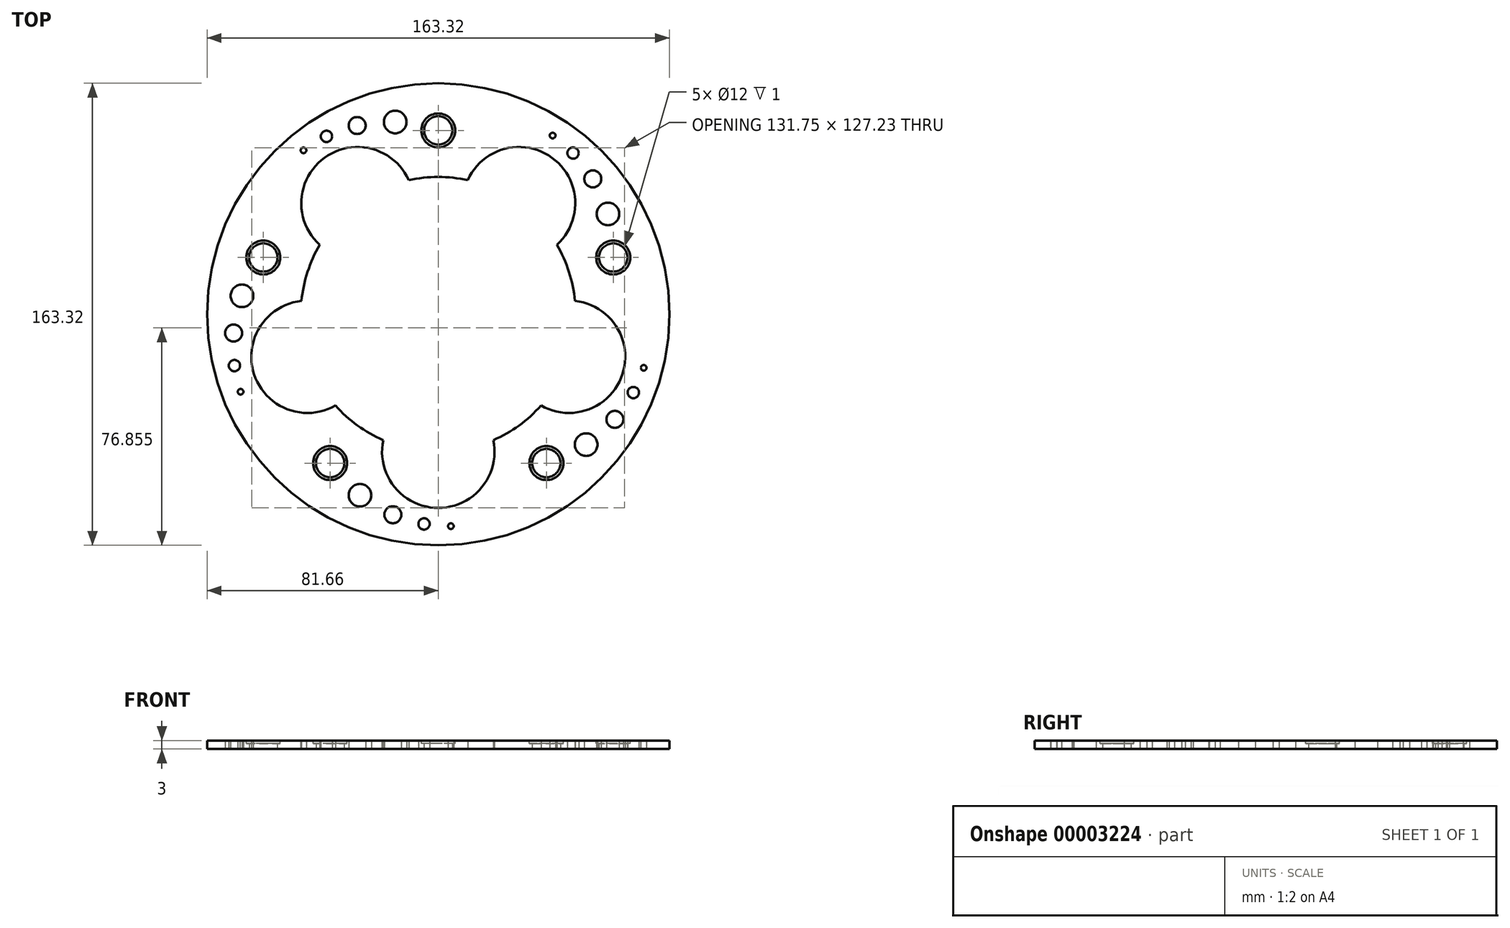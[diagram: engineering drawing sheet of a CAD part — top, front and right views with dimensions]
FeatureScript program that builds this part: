
annotation { "Feature Type Name" : "Feature", "Feature Type Description" : "" }
export const myFeature = defineFeature(function(context is Context, id is Id, definition is map)
    precondition{}
    {
        {
            var Q0;
            Q0=qCreatedBy(makeId("Top.planeOp"),FACE);
            var sketch = newSketch(context, id + "F0", { "sketchPlane" : qUnion([Q0])});
            skCircle(sketch, "E0", {"center": v(0, 0) * mm, "radius": 65 * mm});
            skCircle(sketch, "E1", {"center": v(0, 65) * mm, "radius": 5 * mm});
            skSolve(sketch);
        }
        {
            var Q0;
            {var subQ0=sQuery(id+"F0.wireOp",EDGE,"E1");var subQ1=sQuery(id+"F0.wireOp",EDGE,"E0");var subQ3=makeQuery(id+"F0.imprint","INTERSECT",VERTEX,{"disambiguationData":[OD(0.0)],"derivedFrom":[subQ1,subQ0]});var subQ4=makeQuery(id+"F0.imprint","IMPRINT",EDGE,{"disambiguationData":[TD([[subQ3,1.0]])],"derivedFrom":subQ1});Q0=qUnion([makeQuery(id+"F0.imprint","IMPRINT",FACE,{"disambiguationData":[TD([[subQ4,-1.0]])]}),makeQuery(id+"F0.imprint","IMPRINT",FACE,{"disambiguationData":[TD([[makeQuery(id+"F0.imprint","IMPRINT",EDGE,{"disambiguationData":[TD([[subQ3,-1.0]])],"derivedFrom":subQ1}),1.0]])]}),makeQuery(id+"F0.imprint","IMPRINT",FACE,{"disambiguationData":[TD([[subQ4,1.0]])]})]);}
            var sketch = newSketch(context, id + "F1", { "sketchPlane" : qUnion([Q0])});
            skArc(sketch, "E2", {"start": v(-41.88, 24.57) * mm, "mid": v(-46.18, 15) * mm, "end": v(-48.32, 4.74) * mm});
            skCircle(sketch, "E3", {"center": v(0, 0) * mm, "radius": 81.66 * mm});
            skArc(sketch, "E4", {"start": v(41.88, 24.57) * mm, "mid": v(40.22, 55.35) * mm, "end": v(10.42, 47.42) * mm});
            skArc(sketch, "E5.0.MirrorC", {"start": v(-41.88, 24.57) * mm, "mid": v(-40.22, 55.35) * mm, "end": v(-10.42, 47.42) * mm});
            skArc(sketch, "E6.0.MirrorC", {"start": v(-19.44, -44.5) * mm, "mid": v(0, -68.42) * mm, "end": v(19.44, -44.5) * mm});
            skArc(sketch, "E7.0.MirrorC", {"start": v(48.32, 4.74) * mm, "mid": v(65.07, -21.14) * mm, "end": v(36.3, -32.24) * mm});
            skArc(sketch, "E8.0.MirrorC", {"start": v(-36.3, -32.24) * mm, "mid": v(-65.07, -21.14) * mm, "end": v(-48.32, 4.74) * mm});
            skArc(sketch, "E9.trimOffspring", {"start": v(-36.3, -32.24) * mm, "mid": v(-28.54, -39.28) * mm, "end": v(-19.44, -44.5) * mm});
            skArc(sketch, "E10.trimOffspring", {"start": v(19.44, -44.5) * mm, "mid": v(28.54, -39.28) * mm, "end": v(36.3, -32.24) * mm});
            skArc(sketch, "E11.trimOffspring", {"start": v(48.32, 4.74) * mm, "mid": v(46.18, 15) * mm, "end": v(41.88, 24.57) * mm});
            skArc(sketch, "E12.trimOffspring", {"start": v(10.42, 47.42) * mm, "mid": v(0, 48.56) * mm, "end": v(-10.42, 47.42) * mm});
            skPoint(sketch, "E13.orphan", {"position": v(0, 103.8) * mm});
            skLineSegment(sketch, "E14", {"start": v(0, 0) * mm, "end": v(0, 65) * mm});
            skCircle(sketch, "E15", {"center": v(0, 65) * mm, "radius": 5 * mm});
            skCircle(sketch, "E16", {"center": v(-17.26, 17.2) * mm, "radius": 50.82 * mm, "construction": true});
            skCircle(sketch, "E17", {"center": v(-15.21, 67.98) * mm, "radius": 4 * mm});
            skCircle(sketch, "E18", {"center": v(-28.65, 66.73) * mm, "radius": 3 * mm});
            skCircle(sketch, "E19", {"center": v(-39.5, 62.9) * mm, "radius": 2 * mm});
            skCircle(sketch, "E20", {"center": v(-47.61, 57.96) * mm, "radius": 1 * mm});
            skPoint(sketch, "E21.orphan", {"position": v(-51.3, 63.54) * mm});
            skPoint(sketch, "E22.trimOffspring.end.orphan", {"position": v(-49.46, 60.75) * mm});
            skLineSegment(sketch, "E23", {"start": v(0, 0) * mm, "end": v(28.54, 39.28) * mm});
            skLineSegment(sketch, "E24", {"start": v(0, 0) * mm, "end": v(-28.54, 39.28) * mm});
            skLineSegment(sketch, "E25", {"start": v(0, 0) * mm, "end": v(-46.18, -15) * mm});
            skLineSegment(sketch, "E26", {"start": v(0, 0) * mm, "end": v(46.18, -15) * mm});
            skLineSegment(sketch, "E27", {"start": v(0, 0) * mm, "end": v(0, -48.56) * mm});
            skSolve(sketch);
        }
        {
            var Q0;
            {var subQ5=sQuery(id+"F1.wireOp",EDGE,"E14");var subQ7=sQuery(id+"F1.wireOp",EDGE,"E15");var subQ9=makeQuery(id+"F1.imprint","INTERSECT",VERTEX,{"derivedFrom":[subQ5,subQ7]});Q0=makeQuery(id+"F1.imprint","IMPRINT",FACE,{"disambiguationData":[TD([[makeQuery(id+"F1.imprint","IMPRINT",EDGE,{"disambiguationData":[TD([[subQ9,-1.0]])],"derivedFrom":subQ5}),1.0]])]});}
            var Q1;
            {var subQ0=sQuery(id+"F0.wireOp",EDGE,"E0");var subQ1=sQuery(id+"F0.wireOp",EDGE,"E1");var subQ3=makeQuery(id+"F0.imprint","INTERSECT",VERTEX,{"disambiguationData":[OD(0.0)],"derivedFrom":[subQ0,subQ1]});var subQ4=makeQuery(id+"F0.imprint","IMPRINT",EDGE,{"disambiguationData":[TD([[subQ3,1.0]])],"derivedFrom":subQ0});var subQ5=makeQuery(id+"F1.imprint","INTERSECT",VERTEX,{"derivedFrom":[subQ4,sQuery(id+"F1.wireOp",EDGE,"E14")]});Q1=makeQuery(id+"F1.imprint","IMPRINT",FACE,{"disambiguationData":[TD([[makeQuery(id+"F1.imprint","IMPRINT",EDGE,{"disambiguationData":[TD([[subQ5,-1.0]])],"derivedFrom":subQ4}),-1.0]])]});}
            var Q2;
            {var subQ5=sQuery(id+"F1.wireOp",EDGE,"E14");var subQ7=sQuery(id+"F1.wireOp",EDGE,"E15");var subQ9=makeQuery(id+"F1.imprint","INTERSECT",VERTEX,{"derivedFrom":[subQ5,subQ7]});Q2=makeQuery(id+"F1.imprint","IMPRINT",FACE,{"disambiguationData":[TD([[makeQuery(id+"F1.imprint","IMPRINT",EDGE,{"disambiguationData":[TD([[subQ9,-1.0]])],"derivedFrom":subQ5}),-1.0]])]});}
            var Q3;
            Q3=makeQuery(id+"F1.imprint","IMPRINT",FACE,{"disambiguationData":[TD([[makeQuery(id+"F1.imprint","IMPRINT",EDGE,{"derivedFrom":sQuery(id+"F1.wireOp",EDGE,"E17")}),1.0]])]});
            var Q4;
            Q4=makeQuery(id+"F1.imprint","IMPRINT",FACE,{"disambiguationData":[TD([[makeQuery(id+"F1.imprint","IMPRINT",EDGE,{"derivedFrom":sQuery(id+"F1.wireOp",EDGE,"E18")}),1.0]])]});
            var Q5;
            Q5=makeQuery(id+"F1.imprint","IMPRINT",FACE,{"disambiguationData":[TD([[makeQuery(id+"F1.imprint","IMPRINT",EDGE,{"derivedFrom":sQuery(id+"F1.wireOp",EDGE,"E19")}),1.0]])]});
            var Q6;
            Q6=makeQuery(id+"F1.imprint","IMPRINT",FACE,{"disambiguationData":[TD([[makeQuery(id+"F1.imprint","IMPRINT",EDGE,{"derivedFrom":sQuery(id+"F1.wireOp",EDGE,"E20")}),1.0]])]});
            extrude(context, id + "F2", {"entities" : qUnion([Q0, Q1, Q2, Q3, Q4, Q5, Q6]), "depth" : 25 * mm});
        }
        {
            var Q0;
            Q0=makeQuery(id+"F2.opExtrude","SWEPT_BODY",BODY,{"disambiguationData":[OSD([sQuery(id+"F1.wireOp",EDGE,"E15")])]});
            var Q1;
            Q1=makeQuery(id+"F2.opExtrude","SWEPT_BODY",BODY,{"disambiguationData":[OSD([sQuery(id+"F1.wireOp",EDGE,"E17")])]});
            var Q2;
            Q2=makeQuery(id+"F2.opExtrude","SWEPT_BODY",BODY,{"disambiguationData":[OSD([sQuery(id+"F1.wireOp",EDGE,"E18")])]});
            var Q3;
            Q3=makeQuery(id+"F2.opExtrude","SWEPT_BODY",BODY,{"disambiguationData":[OSD([sQuery(id+"F1.wireOp",EDGE,"E19")])]});
            var Q4;
            Q4=makeQuery(id+"F2.opExtrude","SWEPT_BODY",BODY,{"disambiguationData":[OSD([sQuery(id+"F1.wireOp",EDGE,"E20")])]});
            var Q5;
            Q5=sQuery(id+"F1.wireOp",EDGE,"E3");
            circularPattern(context, id + "F3", {"entities" : qUnion([Q0, Q1, Q2, Q3, Q4]), "axis" : qUnion([Q5]), "angle" : 72 * degree, "instanceCount" : 5});
        }
        {
            var Q0;
            Q0=makeQuery(id+"F1.imprint","IMPRINT",FACE,{"disambiguationData":[TD([[makeQuery(id+"F1.imprint","IMPRINT",EDGE,{"derivedFrom":sQuery(id+"F1.wireOp",EDGE,"E3")}),1.0]])]});
            var Q1;
            {var subQ9=sQuery(id+"F1.wireOp",EDGE,"E4");var subQ11=sQuery(id+"F1.wireOp",EDGE,"E12.trimOffspring");var subQ13=makeQuery(id+"F1.imprint","INTERSECT",VERTEX,{"derivedFrom":[subQ9,subQ11]});Q1=makeQuery(id+"F1.imprint","IMPRINT",FACE,{"disambiguationData":[TD([[makeQuery(id+"F1.imprint","IMPRINT",EDGE,{"disambiguationData":[TD([[subQ13,-1.0]])],"derivedFrom":subQ11}),-1.0]])]});}
            var Q2;
            {var subQ5=sQuery(id+"F1.wireOp",EDGE,"E5.0.MirrorC");var subQ11=sQuery(id+"F1.wireOp",EDGE,"E12.trimOffspring");var subQ13=makeQuery(id+"F1.imprint","INTERSECT",VERTEX,{"derivedFrom":[subQ5,subQ11]});Q2=makeQuery(id+"F1.imprint","IMPRINT",FACE,{"disambiguationData":[TD([[makeQuery(id+"F1.imprint","IMPRINT",EDGE,{"disambiguationData":[TD([[subQ13,1.0]])],"derivedFrom":subQ11}),-1.0]])]});}
            var Q3;
            {var subQ7=sQuery(id+"F1.wireOp",EDGE,"E2");Q3=makeQuery(id+"F1.imprint","IMPRINT",FACE,{"disambiguationData":[TD([[makeQuery(id+"F1.imprint","IMPRINT",EDGE,{"derivedFrom":subQ7}),-1.0]])]});}
            var Q4;
            {var subQ7=sQuery(id+"F1.wireOp",EDGE,"E9.trimOffspring");Q4=makeQuery(id+"F1.imprint","IMPRINT",FACE,{"disambiguationData":[TD([[makeQuery(id+"F1.imprint","IMPRINT",EDGE,{"derivedFrom":subQ7}),-1.0]])]});}
            var Q5;
            {var subQ7=sQuery(id+"F1.wireOp",EDGE,"E10.trimOffspring");Q5=makeQuery(id+"F1.imprint","IMPRINT",FACE,{"disambiguationData":[TD([[makeQuery(id+"F1.imprint","IMPRINT",EDGE,{"derivedFrom":subQ7}),-1.0]])]});}
            var Q6;
            {var subQ7=sQuery(id+"F1.wireOp",EDGE,"E11.trimOffspring");Q6=makeQuery(id+"F1.imprint","IMPRINT",FACE,{"disambiguationData":[TD([[makeQuery(id+"F1.imprint","IMPRINT",EDGE,{"derivedFrom":subQ7}),-1.0]])]});}
            extrude(context, id + "F4", {"entities" : qUnion([Q0, Q1, Q2, Q3, Q4, Q5, Q6]), "depth" : 3 * mm});
        }
        {
            var Q0;
            Q0=makeQuery(id+"F3.opPattern","COPY",BODY,{"derivedFrom":makeQuery(id+"F2.opExtrude","SWEPT_BODY",BODY,{"disambiguationData":[OSD([sQuery(id+"F1.wireOp",EDGE,"E15")])]}),"instanceName":"3"});
            var Q1;
            Q1=makeQuery(id+"F3.opPattern","COPY",BODY,{"derivedFrom":makeQuery(id+"F2.opExtrude","SWEPT_BODY",BODY,{"disambiguationData":[OSD([sQuery(id+"F1.wireOp",EDGE,"E17")])]}),"instanceName":"3"});
            var Q2;
            Q2=makeQuery(id+"F3.opPattern","COPY",BODY,{"derivedFrom":makeQuery(id+"F2.opExtrude","SWEPT_BODY",BODY,{"disambiguationData":[OSD([sQuery(id+"F1.wireOp",EDGE,"E18")])]}),"instanceName":"3"});
            var Q3;
            Q3=makeQuery(id+"F3.opPattern","COPY",BODY,{"derivedFrom":makeQuery(id+"F2.opExtrude","SWEPT_BODY",BODY,{"disambiguationData":[OSD([sQuery(id+"F1.wireOp",EDGE,"E19")])]}),"instanceName":"3"});
            var Q4;
            Q4=makeQuery(id+"F3.opPattern","COPY",BODY,{"derivedFrom":makeQuery(id+"F2.opExtrude","SWEPT_BODY",BODY,{"disambiguationData":[OSD([sQuery(id+"F1.wireOp",EDGE,"E20")])]}),"instanceName":"3"});
            var Q5;
            Q5=makeQuery(id+"F3.opPattern","COPY",BODY,{"derivedFrom":makeQuery(id+"F2.opExtrude","SWEPT_BODY",BODY,{"disambiguationData":[OSD([sQuery(id+"F1.wireOp",EDGE,"E15")])]}),"instanceName":"4"});
            var Q6;
            Q6=makeQuery(id+"F3.opPattern","COPY",BODY,{"derivedFrom":makeQuery(id+"F2.opExtrude","SWEPT_BODY",BODY,{"disambiguationData":[OSD([sQuery(id+"F1.wireOp",EDGE,"E17")])]}),"instanceName":"4"});
            var Q7;
            Q7=makeQuery(id+"F3.opPattern","COPY",BODY,{"derivedFrom":makeQuery(id+"F2.opExtrude","SWEPT_BODY",BODY,{"disambiguationData":[OSD([sQuery(id+"F1.wireOp",EDGE,"E18")])]}),"instanceName":"4"});
            var Q8;
            Q8=makeQuery(id+"F3.opPattern","COPY",BODY,{"derivedFrom":makeQuery(id+"F2.opExtrude","SWEPT_BODY",BODY,{"disambiguationData":[OSD([sQuery(id+"F1.wireOp",EDGE,"E19")])]}),"instanceName":"4"});
            var Q9;
            Q9=makeQuery(id+"F3.opPattern","COPY",BODY,{"derivedFrom":makeQuery(id+"F2.opExtrude","SWEPT_BODY",BODY,{"disambiguationData":[OSD([sQuery(id+"F1.wireOp",EDGE,"E20")])]}),"instanceName":"4"});
            var Q10;
            Q10=makeQuery(id+"F2.opExtrude","SWEPT_BODY",BODY,{"disambiguationData":[OSD([sQuery(id+"F1.wireOp",EDGE,"E15")])]});
            var Q11;
            Q11=makeQuery(id+"F2.opExtrude","SWEPT_BODY",BODY,{"disambiguationData":[OSD([sQuery(id+"F1.wireOp",EDGE,"E17")])]});
            var Q12;
            Q12=makeQuery(id+"F2.opExtrude","SWEPT_BODY",BODY,{"disambiguationData":[OSD([sQuery(id+"F1.wireOp",EDGE,"E18")])]});
            var Q13;
            Q13=makeQuery(id+"F2.opExtrude","SWEPT_BODY",BODY,{"disambiguationData":[OSD([sQuery(id+"F1.wireOp",EDGE,"E19")])]});
            var Q14;
            Q14=makeQuery(id+"F2.opExtrude","SWEPT_BODY",BODY,{"disambiguationData":[OSD([sQuery(id+"F1.wireOp",EDGE,"E20")])]});
            var Q15;
            Q15=makeQuery(id+"F3.opPattern","COPY",BODY,{"derivedFrom":makeQuery(id+"F2.opExtrude","SWEPT_BODY",BODY,{"disambiguationData":[OSD([sQuery(id+"F1.wireOp",EDGE,"E15")])]}),"instanceName":"1"});
            var Q16;
            Q16=makeQuery(id+"F3.opPattern","COPY",BODY,{"derivedFrom":makeQuery(id+"F2.opExtrude","SWEPT_BODY",BODY,{"disambiguationData":[OSD([sQuery(id+"F1.wireOp",EDGE,"E17")])]}),"instanceName":"1"});
            var Q17;
            Q17=makeQuery(id+"F3.opPattern","COPY",BODY,{"derivedFrom":makeQuery(id+"F2.opExtrude","SWEPT_BODY",BODY,{"disambiguationData":[OSD([sQuery(id+"F1.wireOp",EDGE,"E18")])]}),"instanceName":"1"});
            var Q18;
            Q18=makeQuery(id+"F3.opPattern","COPY",BODY,{"derivedFrom":makeQuery(id+"F2.opExtrude","SWEPT_BODY",BODY,{"disambiguationData":[OSD([sQuery(id+"F1.wireOp",EDGE,"E19")])]}),"instanceName":"1"});
            var Q19;
            Q19=makeQuery(id+"F3.opPattern","COPY",BODY,{"derivedFrom":makeQuery(id+"F2.opExtrude","SWEPT_BODY",BODY,{"disambiguationData":[OSD([sQuery(id+"F1.wireOp",EDGE,"E20")])]}),"instanceName":"1"});
            var Q20;
            Q20=makeQuery(id+"F3.opPattern","COPY",BODY,{"derivedFrom":makeQuery(id+"F2.opExtrude","SWEPT_BODY",BODY,{"disambiguationData":[OSD([sQuery(id+"F1.wireOp",EDGE,"E15")])]}),"instanceName":"2"});
            var Q21;
            Q21=makeQuery(id+"F3.opPattern","COPY",BODY,{"derivedFrom":makeQuery(id+"F2.opExtrude","SWEPT_BODY",BODY,{"disambiguationData":[OSD([sQuery(id+"F1.wireOp",EDGE,"E17")])]}),"instanceName":"2"});
            var Q22;
            Q22=makeQuery(id+"F3.opPattern","COPY",BODY,{"derivedFrom":makeQuery(id+"F2.opExtrude","SWEPT_BODY",BODY,{"disambiguationData":[OSD([sQuery(id+"F1.wireOp",EDGE,"E18")])]}),"instanceName":"2"});
            var Q23;
            Q23=makeQuery(id+"F3.opPattern","COPY",BODY,{"derivedFrom":makeQuery(id+"F2.opExtrude","SWEPT_BODY",BODY,{"disambiguationData":[OSD([sQuery(id+"F1.wireOp",EDGE,"E19")])]}),"instanceName":"2"});
            var Q24;
            Q24=makeQuery(id+"F3.opPattern","COPY",BODY,{"derivedFrom":makeQuery(id+"F2.opExtrude","SWEPT_BODY",BODY,{"disambiguationData":[OSD([sQuery(id+"F1.wireOp",EDGE,"E20")])]}),"instanceName":"2"});
            var Q25;
            Q25=makeQuery(id+"F4.opExtrude","SWEPT_BODY",BODY,{"disambiguationData":[OSD([sQuery(id+"F1.wireOp",EDGE,"E2"),sQuery(id+"F1.wireOp",EDGE,"E3"),sQuery(id+"F1.wireOp",EDGE,"E4"),sQuery(id+"F1.wireOp",EDGE,"E5.0.MirrorC"),sQuery(id+"F1.wireOp",EDGE,"E6.0.MirrorC"),sQuery(id+"F1.wireOp",EDGE,"E7.0.MirrorC"),sQuery(id+"F1.wireOp",EDGE,"E8.0.MirrorC"),sQuery(id+"F1.wireOp",EDGE,"E9.trimOffspring"),sQuery(id+"F1.wireOp",EDGE,"E10.trimOffspring"),sQuery(id+"F1.wireOp",EDGE,"E11.trimOffspring"),sQuery(id+"F1.wireOp",EDGE,"E12.trimOffspring"),sQuery(id+"F1.wireOp",EDGE,"E15"),sQuery(id+"F1.wireOp",EDGE,"E17"),sQuery(id+"F1.wireOp",EDGE,"E18"),sQuery(id+"F1.wireOp",EDGE,"E19"),sQuery(id+"F1.wireOp",EDGE,"E20")])]});
            booleanBodies(context, id + "F5", {"operationType" : BooleanOperationType.SUBTRACTION, "tools" : qUnion([Q0, Q1, Q2, Q3, Q4, Q5, Q6, Q7, Q8, Q9, Q10, Q11, Q12, Q13, Q14, Q15, Q16, Q17, Q18, Q19, Q20, Q21, Q22, Q23, Q24]), "targets" : qUnion([Q25])});
        }
        {
            var Q0;
            Q0=makeQuery(id+"F4.opExtrude","CAP_FACE",FACE,{"disambiguationData":[OSD([sQuery(id+"F1.wireOp",EDGE,"E2"),sQuery(id+"F1.wireOp",EDGE,"E3"),sQuery(id+"F1.wireOp",EDGE,"E4"),sQuery(id+"F1.wireOp",EDGE,"E5.0.MirrorC"),sQuery(id+"F1.wireOp",EDGE,"E6.0.MirrorC"),sQuery(id+"F1.wireOp",EDGE,"E7.0.MirrorC"),sQuery(id+"F1.wireOp",EDGE,"E8.0.MirrorC"),sQuery(id+"F1.wireOp",EDGE,"E9.trimOffspring"),sQuery(id+"F1.wireOp",EDGE,"E10.trimOffspring"),sQuery(id+"F1.wireOp",EDGE,"E11.trimOffspring"),sQuery(id+"F1.wireOp",EDGE,"E12.trimOffspring"),sQuery(id+"F1.wireOp",EDGE,"E15"),sQuery(id+"F1.wireOp",EDGE,"E17"),sQuery(id+"F1.wireOp",EDGE,"E18"),sQuery(id+"F1.wireOp",EDGE,"E19"),sQuery(id+"F1.wireOp",EDGE,"E20")])],"isStart":false});
            var sketch = newSketch(context, id + "F6", { "sketchPlane" : qUnion([Q0])});
            skCircle(sketch, "E28", {"center": v(0, 65) * mm, "radius": 6 * mm});
            skSolve(sketch);
        }
        {
            var Q0;
            {var subQ0=makeQuery(id+"F6.imprint","IMPRINT",EDGE,{"derivedFrom":makeQuery(id+"F4.opExtrude","CAP_EDGE",EDGE,{"disambiguationData":[OSD([sQuery(id+"F1.wireOp",EDGE,"E15")])],"isStart":false})});Q0=qUnion([makeQuery(id+"F6.imprint","IMPRINT",FACE,{"disambiguationData":[TD([[subQ0,1.0]])]}),makeQuery(id+"F6.imprint","IMPRINT",FACE,{"disambiguationData":[TD([[makeQuery(id+"F6.imprint","IMPRINT",EDGE,{"derivedFrom":sQuery(id+"F6.wireOp",EDGE,"E28")}),1.0]])]})]);}
            extrude(context, id + "F7", {"entities" : qUnion([Q0]), "oppositeDirection" : true, "depth" : 1 * mm});
        }
        {
            var Q0;
            Q0=makeQuery(id+"F7.opExtrude","SWEPT_BODY",BODY,{"disambiguationData":[OSD([sQuery(id+"F6.wireOp",EDGE,"E28")])]});
            var Q1;
            Q1=makeQuery(id+"F4.opExtrude","CAP_EDGE",EDGE,{"disambiguationData":[OSD([sQuery(id+"F1.wireOp",EDGE,"E3")])],"isStart":false});
            circularPattern(context, id + "F8", {"entities" : qUnion([Q0]), "axis" : qUnion([Q1]), "angle" : 72 * degree, "instanceCount" : 5});
        }
        {
            var Q0;
            Q0=makeQuery(id+"F7.opExtrude","SWEPT_BODY",BODY,{"disambiguationData":[OSD([sQuery(id+"F6.wireOp",EDGE,"E28")])]});
            var Q1;
            Q1=makeQuery(id+"F8.opPattern","COPY",BODY,{"derivedFrom":makeQuery(id+"F7.opExtrude","SWEPT_BODY",BODY,{"disambiguationData":[OSD([sQuery(id+"F6.wireOp",EDGE,"E28")])]}),"instanceName":"1"});
            var Q2;
            Q2=makeQuery(id+"F8.opPattern","COPY",BODY,{"derivedFrom":makeQuery(id+"F7.opExtrude","SWEPT_BODY",BODY,{"disambiguationData":[OSD([sQuery(id+"F6.wireOp",EDGE,"E28")])]}),"instanceName":"2"});
            var Q3;
            Q3=makeQuery(id+"F8.opPattern","COPY",BODY,{"derivedFrom":makeQuery(id+"F7.opExtrude","SWEPT_BODY",BODY,{"disambiguationData":[OSD([sQuery(id+"F6.wireOp",EDGE,"E28")])]}),"instanceName":"3"});
            var Q4;
            Q4=makeQuery(id+"F8.opPattern","COPY",BODY,{"derivedFrom":makeQuery(id+"F7.opExtrude","SWEPT_BODY",BODY,{"disambiguationData":[OSD([sQuery(id+"F6.wireOp",EDGE,"E28")])]}),"instanceName":"4"});
            var Q5;
            Q5=makeQuery(id+"F4.opExtrude","SWEPT_BODY",BODY,{"disambiguationData":[OSD([sQuery(id+"F1.wireOp",EDGE,"E2"),sQuery(id+"F1.wireOp",EDGE,"E3"),sQuery(id+"F1.wireOp",EDGE,"E4"),sQuery(id+"F1.wireOp",EDGE,"E5.0.MirrorC"),sQuery(id+"F1.wireOp",EDGE,"E6.0.MirrorC"),sQuery(id+"F1.wireOp",EDGE,"E7.0.MirrorC"),sQuery(id+"F1.wireOp",EDGE,"E8.0.MirrorC"),sQuery(id+"F1.wireOp",EDGE,"E9.trimOffspring"),sQuery(id+"F1.wireOp",EDGE,"E10.trimOffspring"),sQuery(id+"F1.wireOp",EDGE,"E11.trimOffspring"),sQuery(id+"F1.wireOp",EDGE,"E12.trimOffspring"),sQuery(id+"F1.wireOp",EDGE,"E15"),sQuery(id+"F1.wireOp",EDGE,"E17"),sQuery(id+"F1.wireOp",EDGE,"E18"),sQuery(id+"F1.wireOp",EDGE,"E19"),sQuery(id+"F1.wireOp",EDGE,"E20")])]});
            booleanBodies(context, id + "F9", {"operationType" : BooleanOperationType.SUBTRACTION, "tools" : qUnion([Q0, Q1, Q2, Q3, Q4]), "targets" : qUnion([Q5])});
        }
    });
